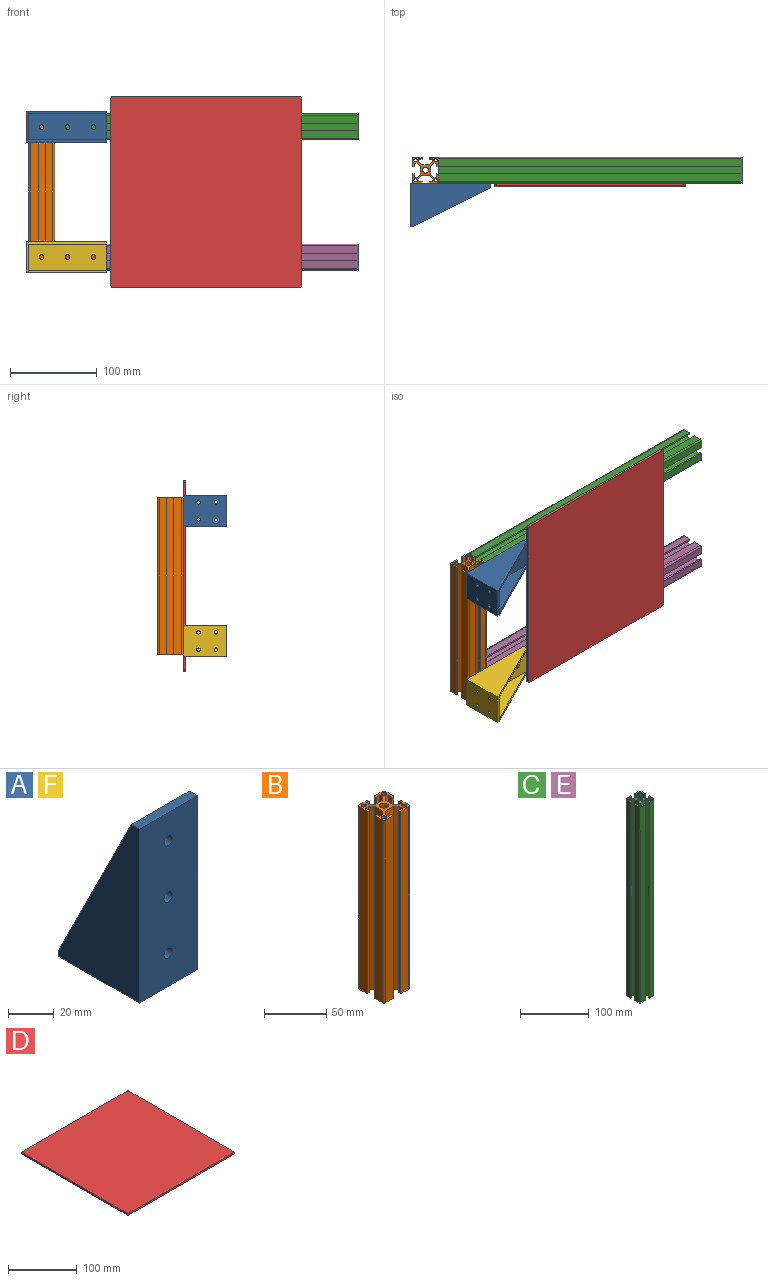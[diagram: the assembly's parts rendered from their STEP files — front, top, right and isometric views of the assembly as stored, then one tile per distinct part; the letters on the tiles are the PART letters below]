
ASSEMBLY  parts=6 mates=5
PART A: 19 faces, bbox 36x50x93 mm
  f0: plane 36x3mm, normal (0,1,0), area 108mm2, adj f5,f6,f13,f14,f17,f18
  f1: cylinder r=2mm len=4mm, axis (0,0,-1), area 37.7mm2, adj f5,f6
  f2: cylinder r=2mm len=4mm, axis (0,0,-1), area 37.7mm2, adj f5,f6
  f3: cylinder r=2mm len=4mm, axis (0,0,-1), area 37.7mm2, adj f5,f6
  f4: cylinder r=2mm len=4mm, axis (0,0,-1), area 37.7mm2, adj f5,f6
  f5: plane 45x30mm, normal (0,0,1), area 1299.7mm2, adj f0,f1,f2,f3,f4,f7,f15,f16
  f6: plane 50x36mm, normal (0,0,-1), area 1749.7mm2, adj f0,f1,f2,f3,f4,f9,f14,f18
  f7: plane 90x30mm, normal (0,1,0), area 2628.7mm2, adj f5,f8,f10,f11,f12,f15,f16
  f8: cylinder r=2.75mm len=5.5mm, axis (0,1,0), area 86.4mm2, adj f7,f9
  f9: plane 93x36mm, normal (0,-1,0), area 3276.7mm2, adj f6,f8,f10,f11,f12,f14,f18
  f10: plane 36x5mm, normal (0,0,1), area 180mm2, adj f7,f9,f13,f14,f17,f18
  f11: cylinder r=2.75mm len=5.5mm, axis (0,-1,0), area 86.4mm2, adj f7,f9
  f12: cylinder r=2.75mm len=5.5mm, axis (0,-1,0), area 86.4mm2, adj f7,f9
  f13: plane 90x45mm, normal (0,0.89,0.45), area 301.9mm2, adj f0,f10,f14,f15
  f14: plane 93x50mm, normal (1,0,0), area 2625mm2, adj f0,f6,f9,f10,f13
  f15: plane 90x45mm, normal (-1,0,0), area 2025mm2, adj f5,f7,f13
  f16: plane 90x45mm, normal (1,0,0), area 2025mm2, adj f5,f7,f17
  f17: plane 90x45mm, normal (0,0.89,0.45), area 301.9mm2, adj f0,f10,f16,f18
  f18: plane 93x50mm, normal (-1,0,0), area 2625mm2, adj f0,f6,f9,f10,f17
PART B: 55 faces, bbox 30x30x180 mm
  f0: plane 180x3.66mm, normal (-0.71,-0.71,0), area 932.8mm2, adj f1,f47,f49,f50
  f1: plane 180x9.17mm, normal (-1,0,0), area 1650.9mm2, adj f0,f2,f49,f50
  f2: plane 180x3.66mm, normal (-0.71,0.71,0), area 932.8mm2, adj f1,f3,f49,f50
  f3: plane 180x3.34mm, normal (0,1,0), area 600.4mm2, adj f2,f4,f49,f50
  f4: plane 180x4.25mm, normal (1,0,0), area 765mm2, adj f3,f5,f49,f50
  f5: plane 180x2mm, normal (0,1,0), area 360mm2, adj f4,f6,f49,f50
  f6: plane 180x9mm, normal (-1,0,0), area 1620mm2, adj f5,f49,f50,f54
  f7: plane 180x9mm, normal (0,-1,0), area 1620mm2, adj f8,f49,f50,f54
  f8: plane 180x2mm, normal (1,0,0), area 360mm2, adj f7,f9,f49,f50
  f9: plane 180x4.25mm, normal (0,1,0), area 765mm2, adj f8,f10,f49,f50
  f10: plane 180x3.34mm, normal (1,0,0), area 600.4mm2, adj f9,f11,f49,f50
  f11: plane 180x3.66mm, normal (0.71,-0.71,0), area 932.8mm2, adj f10,f12,f49,f50
  f12: plane 180x9.17mm, normal (0,-1,0), area 1650.9mm2, adj f11,f13,f49,f50
  f13: plane 180x3.66mm, normal (-0.71,-0.71,0), area 932.8mm2, adj f12,f14,f49,f50
  f14: plane 180x3.34mm, normal (-1,0,0), area 600.4mm2, adj f13,f15,f49,f50
  f15: plane 180x4.25mm, normal (0,1,0), area 765mm2, adj f14,f16,f49,f50
  f16: plane 180x2mm, normal (-1,0,0), area 360mm2, adj f15,f17,f49,f50
  f17: plane 180x9mm, normal (0,-1,0), area 1620mm2, adj f16,f49,f50,f53
  f18: plane 180x9mm, normal (1,0,0), area 1620mm2, adj f19,f49,f50,f53
  f19: plane 180x2mm, normal (0,1,0), area 360mm2, adj f18,f20,f49,f50
  f20: plane 180x4.25mm, normal (-1,0,0), area 765mm2, adj f19,f21,f49,f50
  f21: plane 180x3.34mm, normal (0,1,0), area 600.4mm2, adj f20,f22,f49,f50
  f22: plane 180x3.66mm, normal (0.71,0.71,0), area 932.8mm2, adj f21,f23,f49,f50
  f23: plane 180x9.17mm, normal (1,0,0), area 1650.9mm2, adj f22,f24,f49,f50
  f24: plane 180x3.66mm, normal (0.71,-0.71,0), area 932.8mm2, adj f23,f25,f49,f50
  f25: plane 180x3.34mm, normal (0,-1,0), area 600.4mm2, adj f24,f26,f49,f50
  f26: plane 180x4.25mm, normal (-1,0,0), area 765mm2, adj f25,f27,f49,f50
  f27: plane 180x2mm, normal (0,-1,0), area 360mm2, adj f26,f28,f49,f50
  f28: plane 180x9mm, normal (1,0,0), area 1620mm2, adj f27,f49,f50,f52
  f29: plane 180x9mm, normal (0,1,0), area 1620mm2, adj f30,f49,f50,f52
  f30: plane 180x2mm, normal (-1,0,0), area 360mm2, adj f29,f31,f49,f50
  f31: plane 180x4.25mm, normal (0,-1,0), area 765mm2, adj f30,f32,f49,f50
  f32: plane 180x3.34mm, normal (-1,0,0), area 600.4mm2, adj f31,f33,f49,f50
  f33: plane 180x3.66mm, normal (-0.71,0.71,0), area 932.8mm2, adj f32,f34,f49,f50
  f34: plane 180x9.17mm, normal (0,1,0), area 1650.9mm2, adj f33,f35,f49,f50
  f35: plane 180x3.66mm, normal (0.71,0.71,0), area 932.8mm2, adj f34,f36,f49,f50
  f36: plane 180x3.34mm, normal (1,0,0), area 600.4mm2, adj f35,f37,f49,f50
  f37: plane 180x4.25mm, normal (0,-1,0), area 765mm2, adj f36,f38,f49,f50
  f38: plane 180x2mm, normal (1,0,0), area 360mm2, adj f37,f39,f49,f50
  f39: plane 180x9mm, normal (0,1,0), area 1620mm2, adj f38,f49,f50,f51
  f40: plane 180x9mm, normal (-1,0,0), area 1620mm2, adj f41,f49,f50,f51
  f41: plane 180x2mm, normal (0,-1,0), area 360mm2, adj f40,f42,f49,f50
  f42: plane 180x4.25mm, normal (1,0,0), area 765mm2, adj f41,f47,f49,f50
  f43: cylinder r=2mm len=180mm, axis (0,0,-1), area 2261.9mm2, adj f49,f50
  f44: cylinder r=2mm len=180mm, axis (0,0,-1), area 2261.9mm2, adj f49,f50
  f45: cylinder r=3.4mm len=180mm, axis (0,0,-1), area 3845.3mm2, adj f49,f50
  f46: cylinder r=2mm len=180mm, axis (0,0,-1), area 2261.9mm2, adj f49,f50
  f47: plane 180x3.34mm, normal (0,-1,0), area 600.4mm2, adj f0,f42,f49,f50
  f48: cylinder r=2mm len=180mm, axis (0,0,-1), area 2261.9mm2, adj f49,f50
  f49: plane 30x30mm, normal (0,0,1), area 337.7mm2, adj f0,f1,f2,f3,f4,f5,f6,f7
  f50: plane 30x30mm, normal (0,0,-1), area 337.7mm2, adj f0,f1,f2,f3,f4,f5,f6,f7
  f51: cylinder r=2mm len=180mm, axis (0,0,-1), area 565.5mm2, adj f39,f40,f49,f50
  f52: cylinder r=2mm len=180mm, axis (0,0,1), area 565.5mm2, adj f28,f29,f49,f50
  f53: cylinder r=2mm len=180mm, axis (0,0,-1), area 565.5mm2, adj f17,f18,f49,f50
  f54: cylinder r=2mm len=180mm, axis (0,0,1), area 565.5mm2, adj f6,f7,f49,f50
PART C: 55 faces, bbox 30x30x350 mm
  f0: plane 350x3.66mm, normal (-0.71,-0.71,0), area 1813.7mm2, adj f1,f47,f49,f50
  f1: plane 350x9.17mm, normal (-1,0,0), area 3210.1mm2, adj f0,f2,f49,f50
  f2: plane 350x3.66mm, normal (-0.71,0.71,0), area 1813.7mm2, adj f1,f3,f49,f50
  f3: plane 350x3.34mm, normal (0,1,0), area 1167.5mm2, adj f2,f4,f49,f50
  f4: plane 350x4.25mm, normal (1,0,0), area 1487.5mm2, adj f3,f5,f49,f50
  f5: plane 350x2mm, normal (0,1,0), area 700mm2, adj f4,f6,f49,f50
  f6: plane 350x9mm, normal (-1,0,0), area 3150mm2, adj f5,f49,f50,f54
  f7: plane 350x9mm, normal (0,-1,0), area 3150mm2, adj f8,f49,f50,f54
  f8: plane 350x2mm, normal (1,0,0), area 700mm2, adj f7,f9,f49,f50
  f9: plane 350x4.25mm, normal (0,1,0), area 1487.5mm2, adj f8,f10,f49,f50
  f10: plane 350x3.34mm, normal (1,0,0), area 1167.5mm2, adj f9,f11,f49,f50
  f11: plane 350x3.66mm, normal (0.71,-0.71,0), area 1813.7mm2, adj f10,f12,f49,f50
  f12: plane 350x9.17mm, normal (0,-1,0), area 3210.1mm2, adj f11,f13,f49,f50
  f13: plane 350x3.66mm, normal (-0.71,-0.71,0), area 1813.7mm2, adj f12,f14,f49,f50
  f14: plane 350x3.34mm, normal (-1,0,0), area 1167.5mm2, adj f13,f15,f49,f50
  f15: plane 350x4.25mm, normal (0,1,0), area 1487.5mm2, adj f14,f16,f49,f50
  f16: plane 350x2mm, normal (-1,0,0), area 700mm2, adj f15,f17,f49,f50
  f17: plane 350x9mm, normal (0,-1,0), area 3150mm2, adj f16,f49,f50,f53
  f18: plane 350x9mm, normal (1,0,0), area 3150mm2, adj f19,f49,f50,f53
  f19: plane 350x2mm, normal (0,1,0), area 700mm2, adj f18,f20,f49,f50
  f20: plane 350x4.25mm, normal (-1,0,0), area 1487.5mm2, adj f19,f21,f49,f50
  f21: plane 350x3.34mm, normal (0,1,0), area 1167.5mm2, adj f20,f22,f49,f50
  f22: plane 350x3.66mm, normal (0.71,0.71,0), area 1813.7mm2, adj f21,f23,f49,f50
  f23: plane 350x9.17mm, normal (1,0,0), area 3210.1mm2, adj f22,f24,f49,f50
  f24: plane 350x3.66mm, normal (0.71,-0.71,0), area 1813.7mm2, adj f23,f25,f49,f50
  f25: plane 350x3.34mm, normal (0,-1,0), area 1167.5mm2, adj f24,f26,f49,f50
  f26: plane 350x4.25mm, normal (-1,0,0), area 1487.5mm2, adj f25,f27,f49,f50
  f27: plane 350x2mm, normal (0,-1,0), area 700mm2, adj f26,f28,f49,f50
  f28: plane 350x9mm, normal (1,0,0), area 3150mm2, adj f27,f49,f50,f52
  f29: plane 350x9mm, normal (0,1,0), area 3150mm2, adj f30,f49,f50,f52
  f30: plane 350x2mm, normal (-1,0,0), area 700mm2, adj f29,f31,f49,f50
  f31: plane 350x4.25mm, normal (0,-1,0), area 1487.5mm2, adj f30,f32,f49,f50
  f32: plane 350x3.34mm, normal (-1,0,0), area 1167.5mm2, adj f31,f33,f49,f50
  f33: plane 350x3.66mm, normal (-0.71,0.71,0), area 1813.7mm2, adj f32,f34,f49,f50
  f34: plane 350x9.17mm, normal (0,1,0), area 3210.1mm2, adj f33,f35,f49,f50
  f35: plane 350x3.66mm, normal (0.71,0.71,0), area 1813.7mm2, adj f34,f36,f49,f50
  f36: plane 350x3.34mm, normal (1,0,0), area 1167.5mm2, adj f35,f37,f49,f50
  f37: plane 350x4.25mm, normal (0,-1,0), area 1487.5mm2, adj f36,f38,f49,f50
  f38: plane 350x2mm, normal (1,0,0), area 700mm2, adj f37,f39,f49,f50
  f39: plane 350x9mm, normal (0,1,0), area 3150mm2, adj f38,f49,f50,f51
  f40: plane 350x9mm, normal (-1,0,0), area 3150mm2, adj f41,f49,f50,f51
  f41: plane 350x2mm, normal (0,-1,0), area 700mm2, adj f40,f42,f49,f50
  f42: plane 350x4.25mm, normal (1,0,0), area 1487.5mm2, adj f41,f47,f49,f50
  f43: cylinder r=2mm len=350mm, axis (0,0,-1), area 4398.2mm2, adj f49,f50
  f44: cylinder r=2mm len=350mm, axis (0,0,-1), area 4398.2mm2, adj f49,f50
  f45: cylinder r=3.4mm len=350mm, axis (0,0,-1), area 7477mm2, adj f49,f50
  f46: cylinder r=2mm len=350mm, axis (0,0,-1), area 4398.2mm2, adj f49,f50
  f47: plane 350x3.34mm, normal (0,-1,0), area 1167.5mm2, adj f0,f42,f49,f50
  f48: cylinder r=2mm len=350mm, axis (0,0,-1), area 4398.2mm2, adj f49,f50
  f49: plane 30x30mm, normal (0,0,1), area 337.7mm2, adj f0,f1,f2,f3,f4,f5,f6,f7
  f50: plane 30x30mm, normal (0,0,-1), area 337.7mm2, adj f0,f1,f2,f3,f4,f5,f6,f7
  f51: cylinder r=2mm len=350mm, axis (0,0,-1), area 1099.6mm2, adj f39,f40,f49,f50
  f52: cylinder r=2mm len=350mm, axis (0,0,1), area 1099.6mm2, adj f28,f29,f49,f50
  f53: cylinder r=2mm len=350mm, axis (0,0,-1), area 1099.6mm2, adj f17,f18,f49,f50
  f54: cylinder r=2mm len=350mm, axis (0,0,1), area 1099.6mm2, adj f6,f7,f49,f50
PART D: 10 faces, bbox 220x220x3 mm
  f0: plane 216x3mm, normal (0,-1,0), area 648mm2, adj f4,f5,f6,f9
  f1: plane 216x3mm, normal (1,0,0), area 648mm2, adj f4,f5,f6,f7
  f2: plane 216x3mm, normal (0,1,0), area 648mm2, adj f4,f5,f7,f8
  f3: plane 216x3mm, normal (-1,0,0), area 648mm2, adj f4,f5,f8,f9
  f4: plane 220x220mm, normal (0,0,1), area 48396.6mm2, adj f0,f1,f2,f3,f6,f7,f8,f9
  f5: plane 220x220mm, normal (0,0,-1), area 48396.6mm2, adj f0,f1,f2,f3,f6,f7,f8,f9
  f6: cylinder r=2mm len=3mm, axis (0,0,1), area 9.4mm2, adj f0,f1,f4,f5
  f7: cylinder r=2mm len=3mm, axis (0,0,-1), area 9.4mm2, adj f1,f2,f4,f5
  f8: cylinder r=2mm len=3mm, axis (0,0,1), area 9.4mm2, adj f2,f3,f4,f5
  f9: cylinder r=2mm len=3mm, axis (0,0,-1), area 9.4mm2, adj f0,f3,f4,f5
PART E: same geometry as C
PART F: same geometry as A
PLACE A rot(axis=(-0.71,0,-0.71),180deg) t=(-92.33,-27.01,162.61)mm
PLACE B t=(0.67,15.49,-2.39)mm
PLACE C rot(axis=(0,-1,0),90deg) t=(290.67,15.49,237.61)mm
PLACE D rot(axis=(1,0,0),90deg) t=(115.67,0.49,87.61)mm
PLACE E rot(axis=(0.71,0,0.71),180deg) t=(-59.33,15.49,87.61)mm
PLACE F rot(axis=(-0.71,0,-0.71),180deg) t=(-92.33,-27.01,12.61)mm
MATE fastened A.f8 <-> B.f17  axis (0,1,0) through (-74.33,0.49,162.61)mm
MATE fastened D.f5 <-> C.f7  axis (0,1,0) through (115.67,0.49,87.61)mm
MATE fastened F.f8 <-> B.f17  axis (0,1,0) through (-74.33,0.49,12.61)mm
MATE fastened E.f45 <-> B.f18  axis (-1,0,0) through (-59.33,15.49,12.61)mm
MATE fastened C.f45 <-> B.f18  axis (1,0,0) through (-59.33,15.49,162.61)mm
